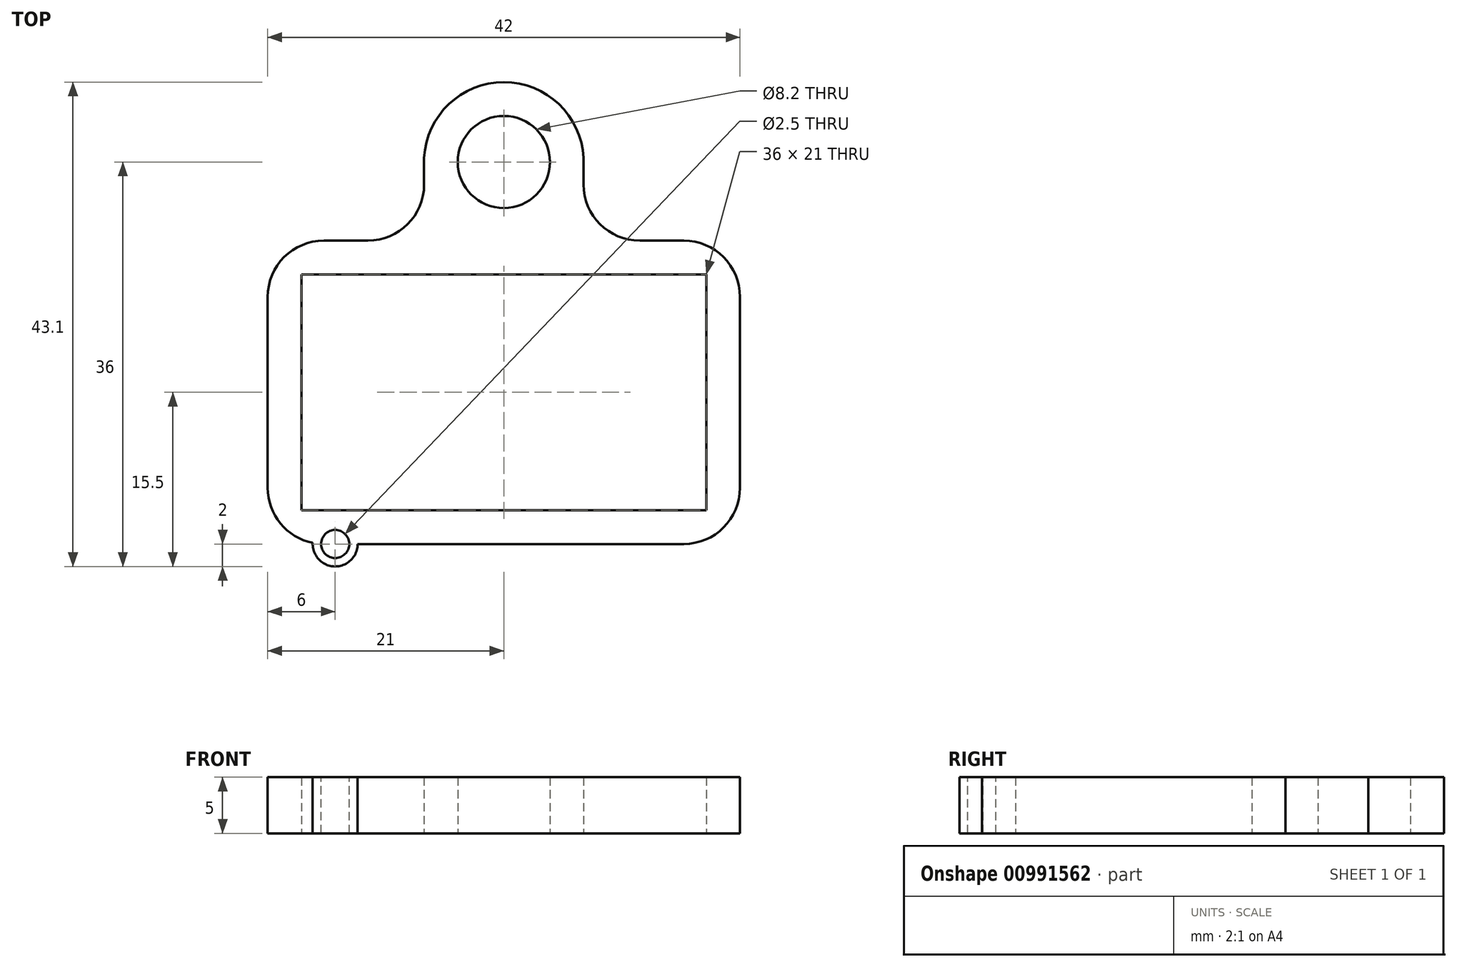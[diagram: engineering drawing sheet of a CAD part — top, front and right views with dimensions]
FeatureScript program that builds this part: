
annotation { "Feature Type Name" : "Feature", "Feature Type Description" : "" }
export const myFeature = defineFeature(function(context is Context, id is Id, definition is map)
    precondition{}
    {
        {
            var Q0;
            Q0=qCreatedBy(makeId("Top.planeOp"),FACE);
            var sketch = newSketch(context, id + "F0", { "sketchPlane" : qUnion([Q0])});
            skLineSegment(sketch, "E0.bottom", {"start": v(18, 10.5) * mm, "end": v(-18, 10.5) * mm});
            skLineSegment(sketch, "E0.top", {"start": v(18, -10.5) * mm, "end": v(-18, -10.5) * mm});
            skLineSegment(sketch, "E0.left", {"start": v(18, 10.5) * mm, "end": v(18, -10.5) * mm});
            skLineSegment(sketch, "E0.right", {"start": v(-18, 10.5) * mm, "end": v(-18, -10.5) * mm});
            skPoint(sketch, "E0.middle", {"position": v(0, 0) * mm});
            skLineSegment(sketch, "E1", {"start": v(-21, 10.5) * mm, "end": v(-21, -13.5) * mm});
            skLineSegment(sketch, "E2", {"start": v(-21, -13.5) * mm, "end": v(21, -13.5) * mm});
            skLineSegment(sketch, "E3", {"start": v(21, -13.5) * mm, "end": v(21, 10.5) * mm});
            skCircle(sketch, "E4", {"center": v(0, 20.5) * mm, "radius": 4.1 * mm});
            skArc(sketch, "E5", {"start": v(7.1, 20.87) * mm, "mid": v(0, 27.6) * mm, "end": v(-7.1, 20.87) * mm});
            skLineSegment(sketch, "E6", {"start": v(-21, 10.5) * mm, "end": v(-21, 13.5) * mm});
            skLineSegment(sketch, "E7", {"start": v(-21, 13.5) * mm, "end": v(-7.1, 13.5) * mm});
            skLineSegment(sketch, "E8", {"start": v(-7.1, 13.5) * mm, "end": v(-7.1, 20.87) * mm});
            skLineSegment(sketch, "E9", {"start": v(7.1, 20.87) * mm, "end": v(7.1, 13.5) * mm});
            skLineSegment(sketch, "E10", {"start": v(7.1, 13.5) * mm, "end": v(21, 13.5) * mm});
            skLineSegment(sketch, "E11", {"start": v(21, 13.5) * mm, "end": v(21, 10.5) * mm});
            skSolve(sketch);
        }
        {
            var Q0;
            Q0=makeQuery(id+"F0.imprint","IMPRINT",FACE,{"disambiguationData":[TD([[makeQuery(id+"F0.imprint","IMPRINT",EDGE,{"derivedFrom":sQuery(id+"F0.wireOp",EDGE,"E0.bottom")}),-1.0]])]});
            extrude(context, id + "F1", {"entities" : qUnion([Q0]), "depth" : 5 * mm, "offsetDistance" : 25 * mm});
        }
        {
            var Q0;
            Q0=makeQuery(id+"F1.opExtrude","SWEPT_EDGE",EDGE,{"disambiguationData":[OSD([sQuery(id+"F0.wireOp",EDGE,"E7"),sQuery(id+"F0.wireOp",EDGE,"E8")])]});
            var Q1;
            Q1=makeQuery(id+"F1.opExtrude","SWEPT_EDGE",EDGE,{"disambiguationData":[OSD([sQuery(id+"F0.wireOp",EDGE,"E9"),sQuery(id+"F0.wireOp",EDGE,"E10")])]});
            var Q2;
            Q2=makeQuery(id+"F1.opExtrude","SWEPT_EDGE",EDGE,{"disambiguationData":[OSD([sQuery(id+"F0.wireOp",EDGE,"E10"),sQuery(id+"F0.wireOp",EDGE,"E11")])]});
            var Q3;
            Q3=makeQuery(id+"F1.opExtrude","SWEPT_EDGE",EDGE,{"disambiguationData":[OSD([sQuery(id+"F0.wireOp",EDGE,"E6"),sQuery(id+"F0.wireOp",EDGE,"E7")])]});
            var Q4;
            Q4=makeQuery(id+"F1.opExtrude","SWEPT_EDGE",EDGE,{"disambiguationData":[OSD([sQuery(id+"F0.wireOp",EDGE,"E1"),sQuery(id+"F0.wireOp",EDGE,"E2")])]});
            var Q5;
            Q5=makeQuery(id+"F1.opExtrude","SWEPT_EDGE",EDGE,{"disambiguationData":[OSD([sQuery(id+"F0.wireOp",EDGE,"E2"),sQuery(id+"F0.wireOp",EDGE,"E3")])]});
            fillet(context, id + "F2", {"entities" : qUnion([Q0, Q1, Q2, Q3, Q4, Q5]), "tangentPropagation" : true, "radius" : 5 * mm, "defaultsChanged" : false, "vertexSettings" : [], "allowEdgeOverflow" : false});
        }
        {
            var Q0;
            Q0=makeQuery(id+"F1.opExtrude","CAP_FACE",FACE,{"disambiguationData":[OSD([sQuery(id+"F0.wireOp",EDGE,"E0.bottom"),sQuery(id+"F0.wireOp",EDGE,"E0.top"),sQuery(id+"F0.wireOp",EDGE,"E0.left"),sQuery(id+"F0.wireOp",EDGE,"E0.right"),sQuery(id+"F0.wireOp",EDGE,"E1"),sQuery(id+"F0.wireOp",EDGE,"E2"),sQuery(id+"F0.wireOp",EDGE,"E3"),sQuery(id+"F0.wireOp",EDGE,"E4"),sQuery(id+"F0.wireOp",EDGE,"E5"),sQuery(id+"F0.wireOp",EDGE,"E6"),sQuery(id+"F0.wireOp",EDGE,"E7"),sQuery(id+"F0.wireOp",EDGE,"E8"),sQuery(id+"F0.wireOp",EDGE,"E9"),sQuery(id+"F0.wireOp",EDGE,"E10"),sQuery(id+"F0.wireOp",EDGE,"E11")])],"isStart":false});
            var sketch = newSketch(context, id + "F3", { "sketchPlane" : qUnion([Q0])});
            skCircle(sketch, "E12", {"center": v(-15, -13.5) * mm, "radius": 2 * mm});
            skSolve(sketch);
        }
        {
            var Q0;
            {var subQ0=sQuery(id+"F3.wireOp",EDGE,"E12");var subQ1=sQuery(id+"F0.wireOp",EDGE,"E2");var subQ5=makeQuery(id+"F1.opExtrude","CAP_EDGE",EDGE,{"disambiguationData":[OSD([subQ1])],"isStart":false});var subQ6=makeQuery(id+"F3.imprint","INTERSECT",VERTEX,{"derivedFrom":[subQ5,subQ0]});Q0=makeQuery(id+"F3.imprint","IMPRINT",FACE,{"disambiguationData":[TD([[makeQuery(id+"F3.imprint","IMPRINT",EDGE,{"disambiguationData":[TD([[subQ6,1.0]])],"derivedFrom":subQ0}),1.0]])]});}
            var Q1;
            Q1=makeQuery(id+"F1.opExtrude","CAP_FACE",FACE,{"disambiguationData":[OSD([sQuery(id+"F0.wireOp",EDGE,"E0.bottom"),sQuery(id+"F0.wireOp",EDGE,"E0.top"),sQuery(id+"F0.wireOp",EDGE,"E0.left"),sQuery(id+"F0.wireOp",EDGE,"E0.right"),sQuery(id+"F0.wireOp",EDGE,"E1"),sQuery(id+"F0.wireOp",EDGE,"E2"),sQuery(id+"F0.wireOp",EDGE,"E3"),sQuery(id+"F0.wireOp",EDGE,"E4"),sQuery(id+"F0.wireOp",EDGE,"E5"),sQuery(id+"F0.wireOp",EDGE,"E6"),sQuery(id+"F0.wireOp",EDGE,"E7"),sQuery(id+"F0.wireOp",EDGE,"E8"),sQuery(id+"F0.wireOp",EDGE,"E9"),sQuery(id+"F0.wireOp",EDGE,"E10"),sQuery(id+"F0.wireOp",EDGE,"E11")])],"isStart":true});
            extrude(context, id + "F4", {"entities" : qUnion([Q0]), "operationType" : NewBodyOperationType.ADD, "endBound" : BoundingType.UP_TO_SURFACE, "oppositeDirection" : true, "depth" : 25 * mm, "endBoundEntityFace" : qUnion([Q1]), "offsetDistance" : 25 * mm});
        }
        {
            var Q0;
            {var subQ0=sQuery(id+"F0.wireOp",EDGE,"E11");var subQ1=sQuery(id+"F0.wireOp",EDGE,"E10");var subQ2=sQuery(id+"F0.wireOp",EDGE,"E9");var subQ3=sQuery(id+"F0.wireOp",EDGE,"E8");var subQ4=sQuery(id+"F0.wireOp",EDGE,"E7");var subQ5=sQuery(id+"F0.wireOp",EDGE,"E6");var subQ6=sQuery(id+"F0.wireOp",EDGE,"E5");var subQ7=sQuery(id+"F0.wireOp",EDGE,"E4");var subQ8=sQuery(id+"F0.wireOp",EDGE,"E3");var subQ9=sQuery(id+"F0.wireOp",EDGE,"E2");var subQ10=sQuery(id+"F0.wireOp",EDGE,"E1");var subQ11=sQuery(id+"F0.wireOp",EDGE,"E0.right");var subQ12=sQuery(id+"F0.wireOp",EDGE,"E0.left");var subQ13=sQuery(id+"F0.wireOp",EDGE,"E0.top");var subQ14=sQuery(id+"F0.wireOp",EDGE,"E0.bottom");Q0=makeQuery(id+"F4.boolean.opBoolean","MERGE",FACE,{"derivedFrom":[makeQuery(id+"F1.opExtrude","CAP_FACE",FACE,{"disambiguationData":[OSD([subQ14,subQ13,subQ12,subQ11,subQ10,subQ9,subQ8,subQ7,subQ6,subQ5,subQ4,subQ3,subQ2,subQ1,subQ0])],"isStart":false}),makeQuery(id+"F4.opExtrude","CAP_FACE",FACE,{"disambiguationData":[OSD([subQ14,subQ13,subQ12,subQ11,subQ10,subQ9,subQ8,subQ7,subQ6,subQ5,subQ4,subQ3,subQ2,subQ1,subQ0,sQuery(id+"F3.wireOp",EDGE,"E12")])],"isStart":true})]});}
            var sketch = newSketch(context, id + "F5", { "sketchPlane" : qUnion([Q0])});
            skCircle(sketch, "E13", {"center": v(-15, -13.5) * mm, "radius": 1.25 * mm});
            skSolve(sketch);
        }
        {
            var Q0;
            Q0=makeQuery(id+"F5.imprint","IMPRINT",FACE,{"disambiguationData":[TD([[makeQuery(id+"F5.imprint","IMPRINT",EDGE,{"derivedFrom":sQuery(id+"F5.wireOp",EDGE,"E13")}),1.0]])]});
            extrude(context, id + "F6", {"entities" : qUnion([Q0]), "operationType" : NewBodyOperationType.REMOVE, "endBound" : BoundingType.UP_TO_NEXT, "oppositeDirection" : true, "depth" : 25 * mm, "offsetDistance" : 25 * mm});
        }
    });
